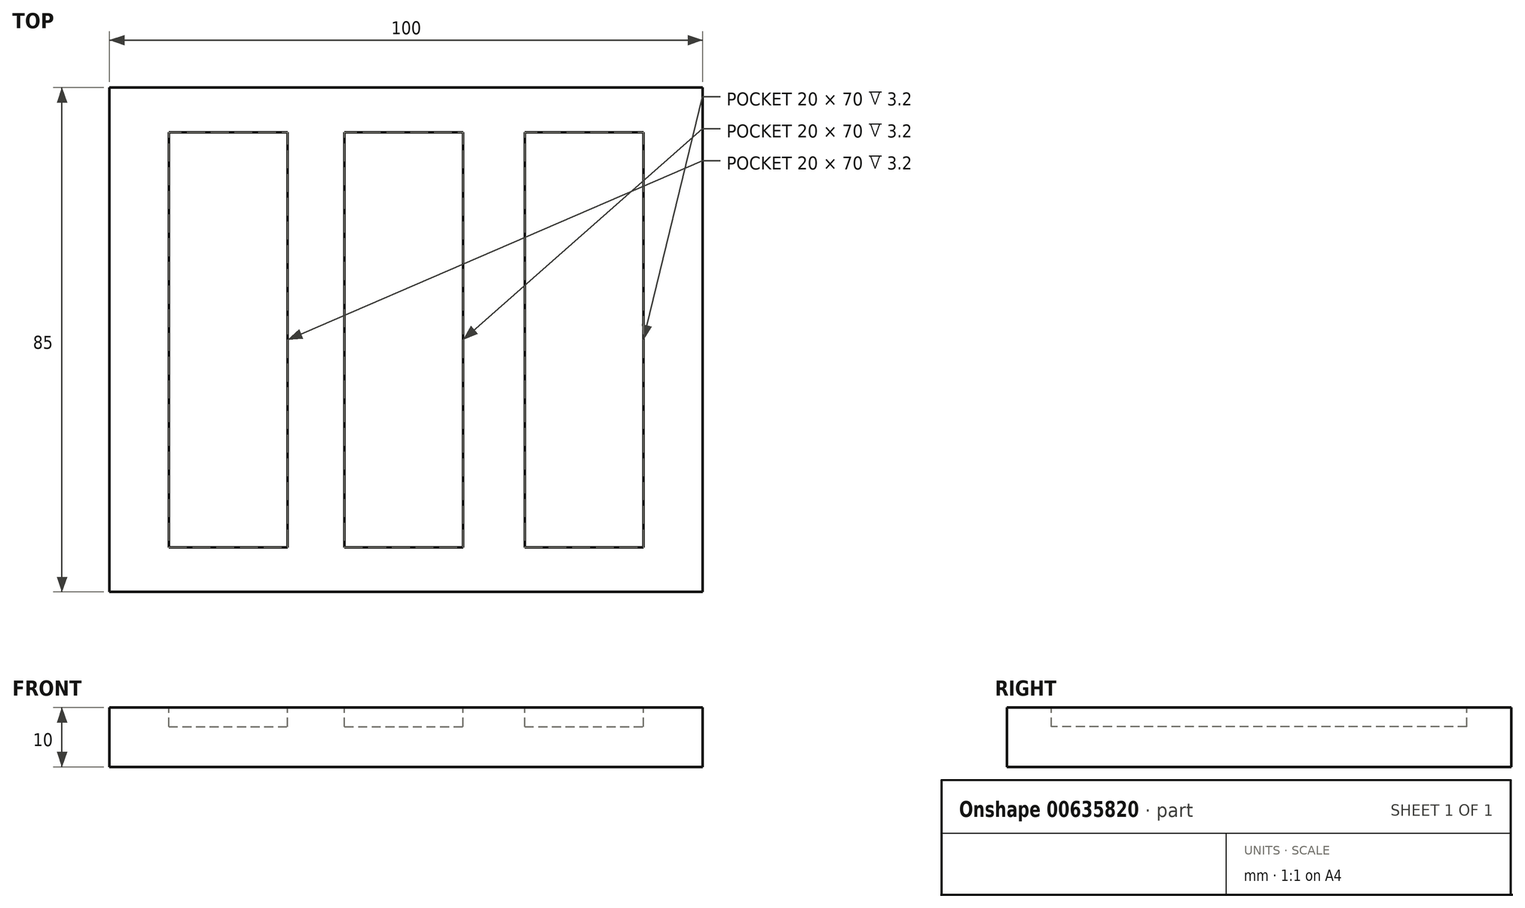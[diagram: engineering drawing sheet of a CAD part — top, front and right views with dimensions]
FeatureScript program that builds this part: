
annotation { "Feature Type Name" : "Feature", "Feature Type Description" : "" }
export const myFeature = defineFeature(function(context is Context, id is Id, definition is map)
    precondition{}
    {
        {
            var Q0;
            Q0=qCreatedBy(makeId("Top.planeOp"),FACE);
            var sketch = newSketch(context, id + "F0", { "sketchPlane" : qUnion([Q0])});
            skLineSegment(sketch, "E0.bottom", {"start": v(-50, 42.5) * mm, "end": v(50, 42.5) * mm});
            skLineSegment(sketch, "E0.top", {"start": v(-50, -42.5) * mm, "end": v(50, -42.5) * mm});
            skLineSegment(sketch, "E0.left", {"start": v(-50, 42.5) * mm, "end": v(-50, -42.5) * mm});
            skLineSegment(sketch, "E0.right", {"start": v(50, 42.5) * mm, "end": v(50, -42.5) * mm});
            skPoint(sketch, "E0.middle", {"position": v(0, 0) * mm});
            skSolve(sketch);
        }
        {
            var Q0;
            Q0=makeQuery(id+"F0.imprint","IMPRINT",FACE,{"disambiguationData":[TD([[makeQuery(id+"F0.imprint","IMPRINT",EDGE,{"derivedFrom":sQuery(id+"F0.wireOp",EDGE,"E0.bottom")}),-1.0]])]});
            extrude(context, id + "F1", {"entities" : qUnion([Q0]), "depth" : 10 * mm, "offsetDistance" : 25 * mm});
        }
        {
            var Q0;
            Q0=qCreatedBy(makeId("Top.planeOp"),FACE);
            var sketch = newSketch(context, id + "F2", { "sketchPlane" : qUnion([Q0])});
            skLineSegment(sketch, "E1", {"start": v(0, 0) * mm, "end": v(0, 55.95) * mm, "construction": true});
            skLineSegment(sketch, "E2", {"start": v(0, 0) * mm, "end": v(0, -56.15) * mm});
            skSolve(sketch);
        }
        {
            var Q0;
            Q0=makeQuery(id+"F1.opExtrude","CAP_FACE",FACE,{"disambiguationData":[OSD([sQuery(id+"F0.wireOp",EDGE,"E0.bottom"),sQuery(id+"F0.wireOp",EDGE,"E0.top"),sQuery(id+"F0.wireOp",EDGE,"E0.left"),sQuery(id+"F0.wireOp",EDGE,"E0.right")])],"isStart":false});
            var sketch = newSketch(context, id + "F3", { "sketchPlane" : qUnion([Q0])});
            skLineSegment(sketch, "E3.bottom", {"start": v(-10.37, 35) * mm, "end": v(9.63, 35) * mm});
            skLineSegment(sketch, "E3.top", {"start": v(-10.37, -35) * mm, "end": v(9.63, -35) * mm});
            skLineSegment(sketch, "E3.left", {"start": v(-10.37, 35) * mm, "end": v(-10.37, -35) * mm});
            skLineSegment(sketch, "E3.right", {"start": v(9.63, 35) * mm, "end": v(9.63, -35) * mm});
            skLineSegment(sketch, "E4.bottom", {"start": v(-40, 35) * mm, "end": v(-20, 35) * mm});
            skLineSegment(sketch, "E4.top", {"start": v(-40, -35) * mm, "end": v(-20, -35) * mm});
            skLineSegment(sketch, "E4.left", {"start": v(-40, 35) * mm, "end": v(-40, -35) * mm});
            skLineSegment(sketch, "E4.right", {"start": v(-20, 35) * mm, "end": v(-20, -35) * mm});
            skLineSegment(sketch, "E5.bottom", {"start": v(20, 35) * mm, "end": v(40, 35) * mm});
            skLineSegment(sketch, "E5.top", {"start": v(20, -35) * mm, "end": v(40, -35) * mm});
            skLineSegment(sketch, "E5.left", {"start": v(20, 35) * mm, "end": v(20, -35) * mm});
            skLineSegment(sketch, "E5.right", {"start": v(40, 35) * mm, "end": v(40, -35) * mm});
            skSolve(sketch);
        }
        {
            var Q0;
            Q0=makeQuery(id+"F3.imprint","IMPRINT",FACE,{"disambiguationData":[TD([[makeQuery(id+"F3.imprint","IMPRINT",EDGE,{"derivedFrom":sQuery(id+"F3.wireOp",EDGE,"E4.bottom")}),-1.0]])]});
            var Q1;
            Q1=makeQuery(id+"F3.imprint","IMPRINT",FACE,{"disambiguationData":[TD([[makeQuery(id+"F3.imprint","IMPRINT",EDGE,{"derivedFrom":sQuery(id+"F3.wireOp",EDGE,"E3.bottom")}),-1.0]])]});
            var Q2;
            Q2=makeQuery(id+"F3.imprint","IMPRINT",FACE,{"disambiguationData":[TD([[makeQuery(id+"F3.imprint","IMPRINT",EDGE,{"derivedFrom":sQuery(id+"F3.wireOp",EDGE,"E5.bottom")}),-1.0]])]});
            extrude(context, id + "F4", {"entities" : qUnion([Q0, Q1, Q2]), "operationType" : NewBodyOperationType.REMOVE, "oppositeDirection" : true, "depth" : 3.2 * mm, "offsetDistance" : 25 * mm});
        }
    });
